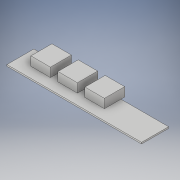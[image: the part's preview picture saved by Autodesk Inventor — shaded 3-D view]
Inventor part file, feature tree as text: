
AUTODESK INVENTOR PART (.ipt)
format: ipt  version: 2018 (Build 220112000, 112)  size: 148,480 bytes
history: native  units: in
note: dims shown in document units (in); Inventor stores cm internally (conversion verified against a paired STEP export)
features: extrude x4, sketch x4
ambient origin geometry x8: Origin, YZ Plane, XZ Plane, XY Plane, X Axis, Y Axis, Z Axis, Center Point
bodies: Solid1 (feature_tree)
feature tree (8):
  extrude  "Extrusion1"  Depth=0.7087in
  extrude  "Extrusion2"  TaperAngle=0.0deg  [1 undecoded]
  extrude  "Extrusion3"  Depth=0.5217in
  extrude  "Extrusion4"  TaperAngle=0.0deg  [1 undecoded]
  sketch  "Sketch1"  dims[d0=3.5335in d1=0.7087in]
  sketch  "Sketch2"  dims[d2=0.0394in d3=0.0in d4=0.0in]
  sketch  "Sketch3"  dims[d5=0.563in d6=0.5217in]
  sketch  "Sketch4"  dims[d7=0.3839in d8=0.0in d9=0.0in d10=0.563in d11=0.5217in d12=0.0689in d13=0.0in d14=0.8661in d15=0.5118in d17=0.1181in d18=0.2756in d19=0.5315in d20=0.5118in d21=0.1969in d22=0.1969in d23=0.5315in d24=0.5118in d25=0.2362in d26=0.0in]
note: 2 required parameter values undecoded (feature->parameter linkage not recoverable at this tier; creation-order binding heuristic only, values carry confidence <= 0.55)
